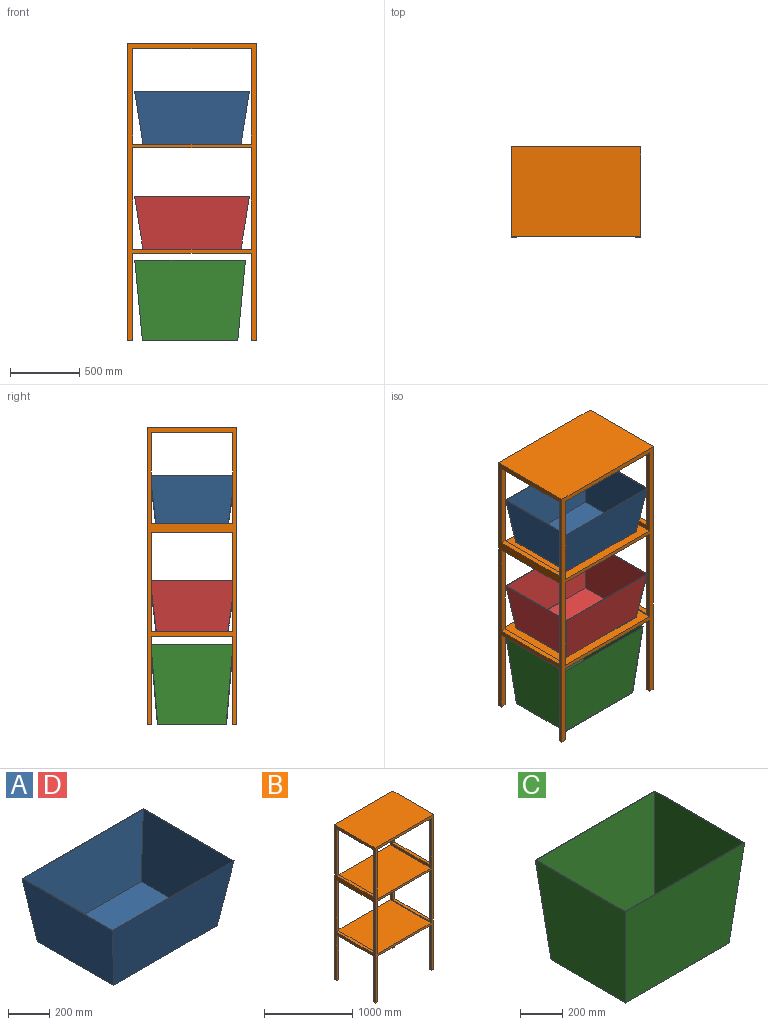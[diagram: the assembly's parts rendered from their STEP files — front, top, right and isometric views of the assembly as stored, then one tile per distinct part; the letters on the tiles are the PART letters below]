
ASSEMBLY  parts=4 mates=3
PART A: 11 faces, bbox 830x620x380 mm
  f0: plane 830x620mm, normal (0,0,1), area 8752.7mm2, adj f2,f3,f4,f5,f7,f8,f9,f10
  f1: plane 710x520mm, normal (0,0,-1), area 369200mm2, adj f2,f3,f4,f5
  f2: plane 620x380mm, normal (0.99,0,-0.16), area 219283.4mm2, adj f0,f1,f4,f5
  f3: plane 620x380mm, normal (-0.99,0,-0.16), area 219283.4mm2, adj f0,f1,f4,f5
  f4: plane 830x380mm, normal (0,0.99,-0.12), area 294644.5mm2, adj f0,f1,f2,f3
  f5: plane 830x380mm, normal (0,-0.99,-0.14), area 295648.9mm2, adj f0,f1,f2,f3
  f6: plane 704.87x514.74mm, normal (0,0,1), area 362824.4mm2, adj f7,f8,f9,f10
  f7: plane 613.95x377mm, normal (-0.99,0,0.16), area 215392.9mm2, adj f0,f6,f9,f10
  f8: plane 613.95x377mm, normal (0.99,0,0.16), area 215392.9mm2, adj f0,f6,f9,f10
  f9: plane 823.93x377mm, normal (0,-0.99,0.12), area 290192.2mm2, adj f0,f6,f7,f8
  f10: plane 823.93x377mm, normal (0,0.99,0.14), area 291181.4mm2, adj f0,f6,f7,f8
PART B: 40 faces, bbox 935x648x2150 mm
  f0: plane 37.5x29mm, normal (0,0,-1), area 1087.5mm2, adj f2,f4,f9,f38
  f1: plane 2150x648mm, normal (-1,0,0), area 204940mm2, adj f3,f9,f10,f12,f13,f19,f26,f27
  f2: plane 2150x648mm, normal (1,0,0), area 204940mm2, adj f0,f9,f10,f11,f12,f19,f23,f24
  f3: plane 37.5x29mm, normal (0,0,-1), area 1087.5mm2, adj f1,f6,f9,f38
  f4: plane 632x29mm, normal (-1,0,0), area 18328mm2, adj f0,f5,f9,f38
  f5: plane 860x29mm, normal (0,0,-1), area 24940mm2, adj f4,f6,f9,f38
  f6: plane 632x29mm, normal (1,0,0), area 18328mm2, adj f3,f5,f9,f38
  f7: plane 732x648mm, normal (1,0,0), area 49536mm2, adj f9,f10,f17,f18,f33,f34,f35,f36
  f8: plane 732x648mm, normal (-1,0,0), area 49536mm2, adj f9,f10,f17,f18,f29,f30,f31,f32
  f9: plane 2150x935mm, normal (0,-1,0), area 243810mm2, adj f0,f1,f2,f3,f4,f5,f6,f7
  f10: plane 2150x935mm, normal (0,1,0), area 243810mm2, adj f1,f2,f7,f8,f11,f12,f13,f14
  f11: plane 37.5x29mm, normal (0,0,-1), area 1087.5mm2, adj f2,f10,f14,f39
  f12: plane 935x648mm, normal (0,0,1), area 605880mm2, adj f1,f2,f9,f10
  f13: plane 37.5x29mm, normal (0,0,-1), area 1087.5mm2, adj f1,f10,f16,f39
  f14: plane 632x29mm, normal (-1,0,0), area 18328mm2, adj f10,f11,f15,f39
  f15: plane 860x29mm, normal (0,0,-1), area 24940mm2, adj f10,f14,f16,f39
  f16: plane 632x29mm, normal (1,0,0), area 18328mm2, adj f10,f13,f15,f39
  f17: plane 860x648mm, normal (0,0,-1), area 557280mm2, adj f7,f8,f9,f10
  f18: plane 860x648mm, normal (0,0,1), area 557280mm2, adj f7,f8,f9,f10
  f19: plane 935x648mm, normal (0,0,-1), area 601530mm2, adj f1,f2,f9,f10,f20,f22,f23,f25
  f20: plane 690x648mm, normal (1,0,0), area 59490mm2, adj f9,f10,f19,f21,f26,f27,f28
  f21: plane 860x648mm, normal (0,0,1), area 557280mm2, adj f9,f10,f20,f22
  f22: plane 690x648mm, normal (-1,0,0), area 59490mm2, adj f9,f10,f19,f21,f23,f24,f25
  f23: plane 657x37.5mm, normal (0,1,0), area 24637.5mm2, adj f2,f19,f22,f24
  f24: plane 590x37.5mm, normal (0,0,1), area 22125mm2, adj f2,f22,f23,f25
  f25: plane 657x37.5mm, normal (0,-1,0), area 24637.5mm2, adj f2,f19,f22,f24
  f26: plane 657x37.5mm, normal (0,-1,0), area 24637.5mm2, adj f1,f19,f20,f27
  f27: plane 590x37.5mm, normal (0,0,1), area 22125mm2, adj f1,f20,f26,f28
  f28: plane 657x37.5mm, normal (0,1,0), area 24637.5mm2, adj f1,f19,f20,f27
  f29: plane 720x37.5mm, normal (0,1,0), area 27000mm2, adj f2,f8,f30,f32
  f30: plane 590x37.5mm, normal (0,0,1), area 22125mm2, adj f2,f8,f29,f31
  f31: plane 720x37.5mm, normal (0,-1,0), area 27000mm2, adj f2,f8,f30,f32
  f32: plane 590x37.5mm, normal (0,0,-1), area 22125mm2, adj f2,f8,f29,f31
  f33: plane 590x37.5mm, normal (0,0,-1), area 22125mm2, adj f1,f7,f34,f36
  f34: plane 720x37.5mm, normal (0,-1,0), area 27000mm2, adj f1,f7,f33,f35
  f35: plane 590x37.5mm, normal (0,0,1), area 22125mm2, adj f1,f7,f34,f36
  f36: plane 720x37.5mm, normal (0,1,0), area 27000mm2, adj f1,f7,f33,f35
  f37: plane 935x590mm, normal (0,0,-1), area 551650mm2, adj f1,f2,f38,f39
  f38: plane 935x637mm, normal (0,1,0), area 52075mm2, adj f0,f1,f2,f3,f4,f5,f6,f37
  f39: plane 935x637mm, normal (0,-1,0), area 52075mm2, adj f1,f2,f11,f13,f14,f15,f16,f37
PART C: 11 faces, bbox 800x600x580 mm
  f0: plane 800x600mm, normal (0,0,1), area 8397.7mm2, adj f2,f3,f4,f5,f7,f8,f9,f10
  f1: plane 690x500mm, normal (0,0,-1), area 345000mm2, adj f2,f3,f4,f5
  f2: plane 800x580mm, normal (0,1,-0.09), area 433702.6mm2, adj f0,f1,f4,f5
  f3: plane 800x580mm, normal (0,-1,-0.09), area 433702.6mm2, adj f0,f1,f4,f5
  f4: plane 600x580mm, normal (1,0,-0.09), area 320431.1mm2, adj f0,f1,f2,f3
  f5: plane 600x580mm, normal (-1,0,-0.09), area 320431.1mm2, adj f0,f1,f2,f3
  f6: plane 684.54x494.5mm, normal (0,0,1), area 338502.6mm2, adj f7,f8,f9,f10
  f7: plane 793.97x577mm, normal (0,-1,0.09), area 428133.7mm2, adj f0,f6,f9,f10
  f8: plane 793.97x577mm, normal (0,1,0.09), area 428133.7mm2, adj f0,f6,f9,f10
  f9: plane 593.98x577mm, normal (-1,0,0.09), area 315433.1mm2, adj f0,f6,f7,f8
  f10: plane 593.98x577mm, normal (1,0,0.09), area 315433.1mm2, adj f0,f6,f7,f8
PART D: same geometry as A
PLACE A t=(640.92,1478.39,1484.14)mm
PLACE B t=(173.42,849.39,62.14)mm fixed
PLACE C t=(682.15,1473.89,62.14)mm
PLACE D t=(640.92,1478.39,724.14)mm
MATE planar A.f1 <-> B.f21  axis (0,0,-1) through (640.92,1173.39,1484.14)mm
MATE planar C.f1 <-> B.f13  axis (0,0,-1) through (627.17,1173.89,62.14)mm
MATE planar D.f1 <-> B.f18  axis (0,0,-1) through (640.92,1173.39,724.14)mm
